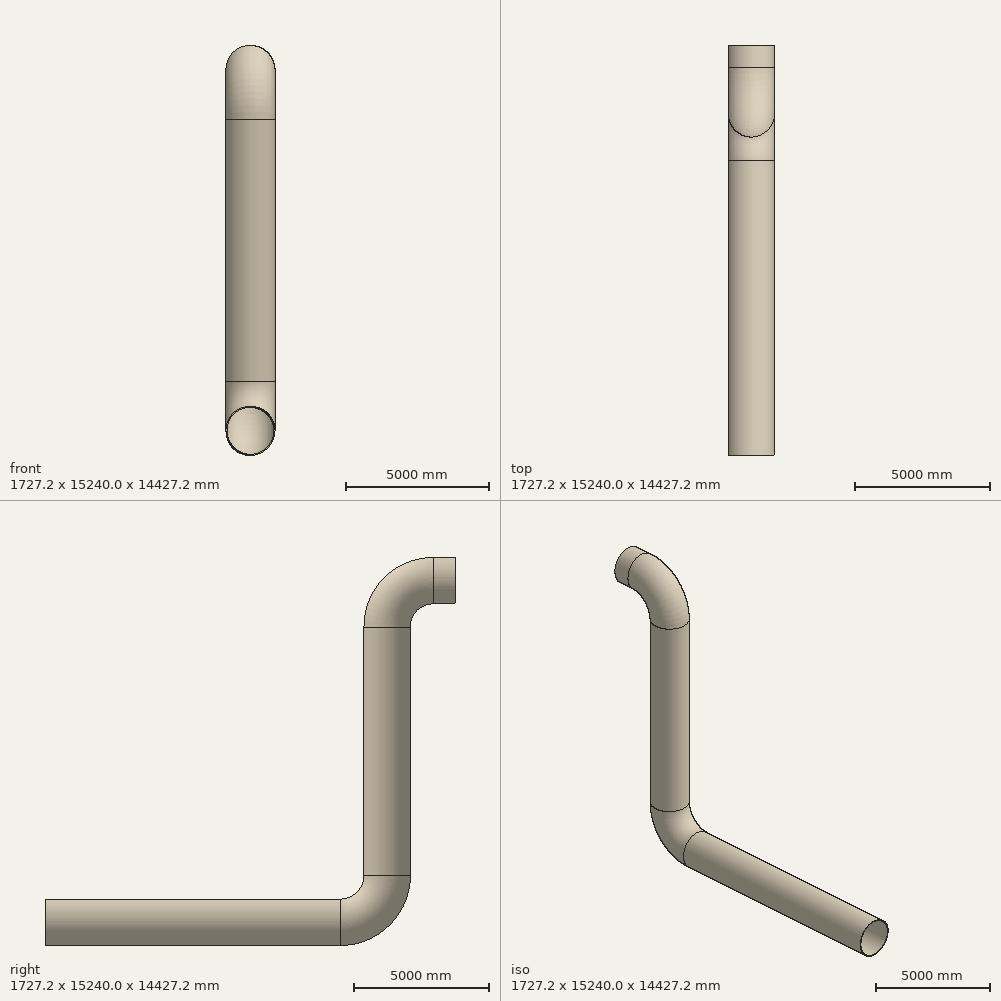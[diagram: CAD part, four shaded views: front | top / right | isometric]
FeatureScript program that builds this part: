
annotation { "Feature Type Name" : "Feature", "Feature Type Description" : "" }
export const myFeature = defineFeature(function(context is Context, id is Id, definition is map)
    precondition{}
    {
        {
            var Q0;
            Q0=qCreatedBy(makeId("Front.planeOp"),FACE);
            var sketch = newSketch(context, id + "F0", { "sketchPlane" : qUnion([Q0])});
            skCircle(sketch, "E0", {"center": v(0, 0) * mm, "radius": 863.6 * mm});
            skCircle(sketch, "E1", {"center": v(0, 0) * mm, "radius": 825.5 * mm});
            skSolve(sketch);
        }
        {
            var Q0;
            Q0=qCreatedBy(makeId("Right.planeOp"),FACE);
            var sketch = newSketch(context, id + "F1", { "sketchPlane" : qUnion([Q0])});
            skLineSegment(sketch, "E2", {"start": v(0, 0) * mm, "end": v(-812.8, 0) * mm});
            skLineSegment(sketch, "E3", {"start": v(-2540, -1727.2) * mm, "end": v(-2540, -10972.8) * mm});
            skLineSegment(sketch, "E4", {"start": v(-4267.2, -12700) * mm, "end": v(-15240, -12700) * mm});
            skPoint(sketch, "E5.visualSharp", {"position": v(-2540, 0) * mm});
            skArc(sketch, "E5.filletArc", {"start": v(-812.8, 0) * mm, "mid": v(-2034.11, -505.89) * mm, "end": v(-2540, -1727.2) * mm});
            skPoint(sketch, "E6.visualSharp", {"position": v(-2540, -12700) * mm});
            skArc(sketch, "E6.filletArc", {"start": v(-4267.2, -12700) * mm, "mid": v(-3045.89, -12194.11) * mm, "end": v(-2540, -10972.8) * mm});
            skSolve(sketch);
        }
        {
            var Q0;
            Q0=makeQuery(id+"F0.imprint","IMPRINT",FACE,{"disambiguationData":[TD([[makeQuery(id+"F0.imprint","IMPRINT",EDGE,{"derivedFrom":sQuery(id+"F0.wireOp",EDGE,"E0")}),1.0]])]});
            var Q1;
            Q1=sQuery(id+"F1.wireOp",EDGE,"E2");
            var Q2;
            Q2=sQuery(id+"F1.wireOp",EDGE,"E5.filletArc");
            var Q3;
            Q3=sQuery(id+"F1.wireOp",EDGE,"E3");
            var Q4;
            Q4=sQuery(id+"F1.wireOp",EDGE,"E6.filletArc");
            var Q5;
            Q5=sQuery(id+"F1.wireOp",EDGE,"E4");
            sweep(context, id + "F2", {"profiles" : qUnion([Q0]), "path" : qUnion([Q1, Q2, Q3, Q4, Q5])});
        }
    });
